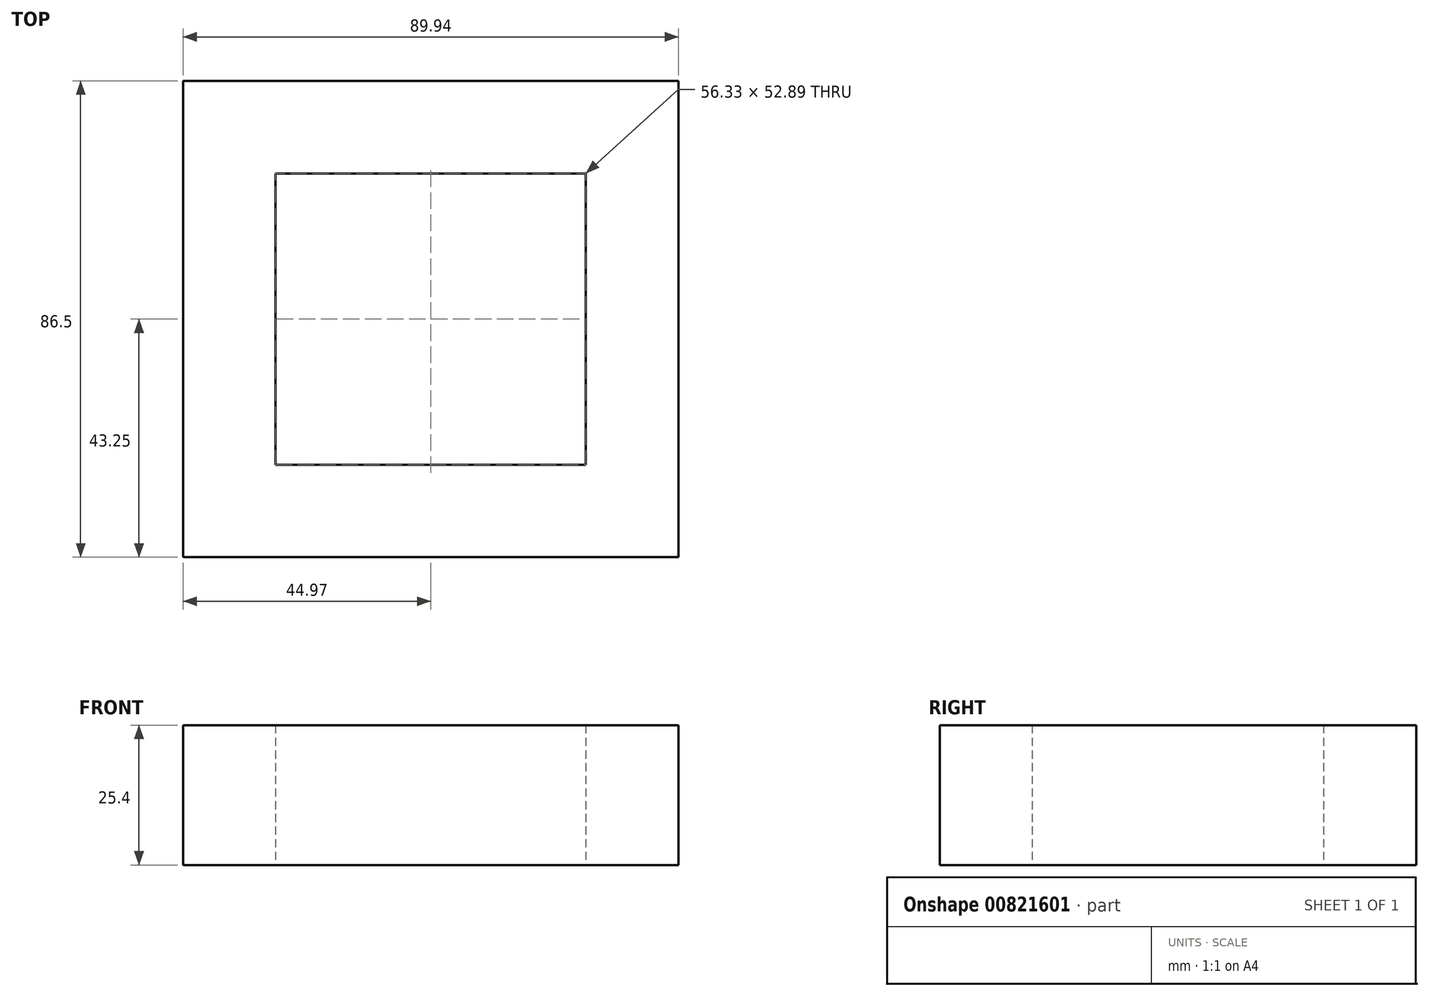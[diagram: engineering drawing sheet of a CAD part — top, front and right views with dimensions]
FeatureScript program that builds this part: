
annotation { "Feature Type Name" : "Feature", "Feature Type Description" : "" }
export const myFeature = defineFeature(function(context is Context, id is Id, definition is map)
    precondition{}
    {
        {
            var Q0;
            Q0=qCreatedBy(makeId("Top.planeOp"),FACE);
            var sketch = newSketch(context, id + "F0", { "sketchPlane" : qUnion([Q0])});
            skLineSegment(sketch, "E0.bottom", {"start": v(44.97, 43.25) * mm, "end": v(-44.97, 43.25) * mm});
            skLineSegment(sketch, "E0.top", {"start": v(44.97, -43.25) * mm, "end": v(-44.97, -43.25) * mm});
            skLineSegment(sketch, "E0.left", {"start": v(44.97, 43.25) * mm, "end": v(44.97, -43.25) * mm});
            skLineSegment(sketch, "E0.right", {"start": v(-44.97, 43.25) * mm, "end": v(-44.97, -43.25) * mm});
            skPoint(sketch, "E0.middle", {"position": v(0, 0) * mm});
            skLineSegment(sketch, "E1.bottom", {"start": v(28.17, 26.45) * mm, "end": v(-28.17, 26.45) * mm});
            skLineSegment(sketch, "E1.top", {"start": v(28.17, -26.45) * mm, "end": v(-28.17, -26.45) * mm});
            skLineSegment(sketch, "E1.left", {"start": v(28.17, 26.45) * mm, "end": v(28.17, -26.45) * mm});
            skLineSegment(sketch, "E1.right", {"start": v(-28.17, 26.45) * mm, "end": v(-28.17, -26.45) * mm});
            skSolve(sketch);
        }
        {
            var Q0;
            Q0 = qSketchRegion(id + "F0", true);
            extrude(context, id + "F1", {"entities" : qUnion([Q0]), "endBound" : BoundingType.SYMMETRIC, "depth" : 25.4 * mm, "offsetDistance" : 25.4 * mm});
        }
    });
